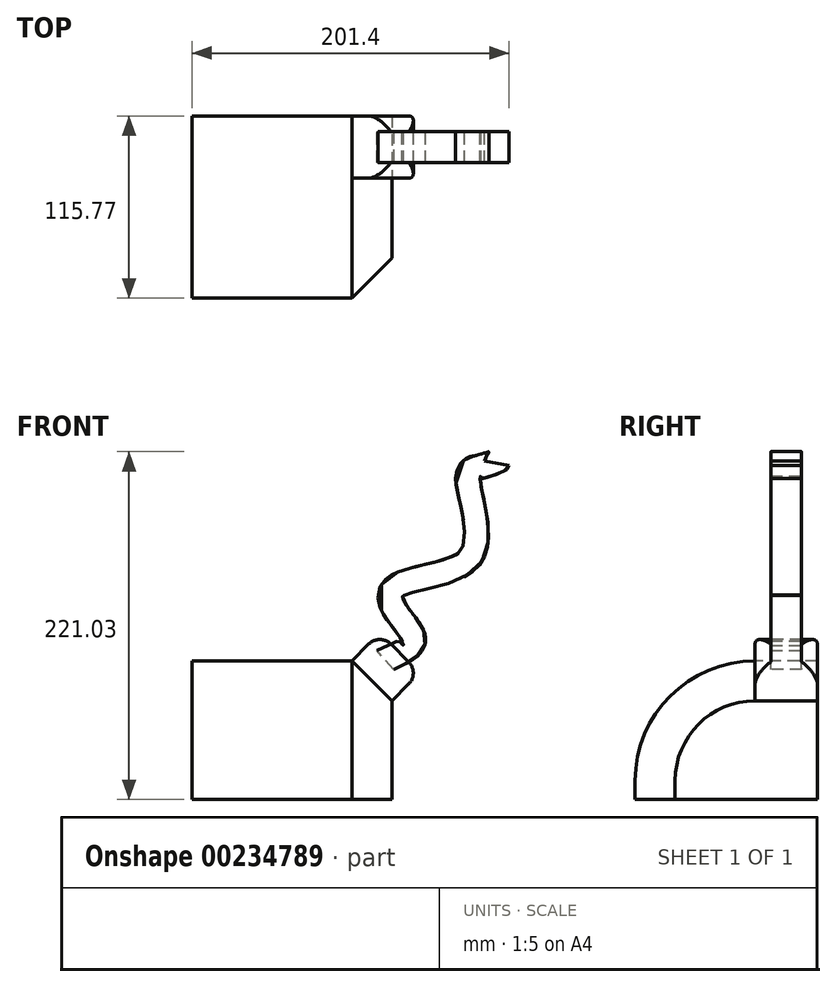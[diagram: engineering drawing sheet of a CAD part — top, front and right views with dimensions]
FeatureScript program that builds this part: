
annotation { "Feature Type Name" : "Feature", "Feature Type Description" : "" }
export const myFeature = defineFeature(function(context is Context, id is Id, definition is map)
    precondition{}
    {
        {
            var Q0;
            Q0=qCreatedBy(makeId("Top.planeOp"),FACE);
            var sketch = newSketch(context, id + "F0", { "sketchPlane" : qUnion([Q0])});
            skLineSegment(sketch, "E0.bottom", {"start": v(-62.89, 58.9) * mm, "end": v(64.11, 58.9) * mm});
            skLineSegment(sketch, "E0.top", {"start": v(-62.89, -56.86) * mm, "end": v(64.11, -56.86) * mm});
            skLineSegment(sketch, "E0.left", {"start": v(-62.89, 58.9) * mm, "end": v(-62.89, -56.86) * mm});
            skLineSegment(sketch, "E0.right", {"start": v(64.11, 58.9) * mm, "end": v(64.11, -56.86) * mm});
            skSolve(sketch);
        }
        {
            var Q0;
            Q0 = qSketchRegion(id + "F0", true);
            extrude(context, id + "F1", {"entities" : qUnion([Q0]), "depth" : 88.14 * mm});
        }
        {
            var Q0;
            Q0=makeQuery(id+"F1.opExtrude","CAP_EDGE",EDGE,{"disambiguationData":[OSD([sQuery(id+"F0.wireOp",EDGE,"E0.top")])],"isStart":false});
            fillet(context, id + "F2", {"entities" : qUnion([Q0]), "radius" : 76.2 * mm, "tangentPropagation" : true, "allowEdgeOverflow" : false});
        }
        {
            var Q0;
            Q0=makeQuery(id+"F1.opExtrude","CAP_EDGE",EDGE,{"disambiguationData":[OSD([sQuery(id+"F0.wireOp",EDGE,"E0.right")])],"isStart":false});
            chamfer(context, id + "F3", {"entities" : qUnion([Q0]), "width" : 25.4 * mm, "tangentPropagation" : true});
        }
        {
            var Q0;
            Q0=makeQuery(id+"F3.opChamfer","BLEND_FACE",FACE,{"disambiguationData":[OSD([sQuery(id+"F0.wireOp",EDGE,"E0.right")])]});
            extrude(context, id + "F4", {"entities" : qUnion([Q0]), "operationType" : NewBodyOperationType.ADD, "depth" : 25 * mm, "hasDraft" : true, "draftAngle" : 0 * degree});
        }
        {
            var Q0;
            Q0=makeQuery(id+"F4.opExtrude","CAP_EDGE",EDGE,{"disambiguationData":[OSD([sQuery(id+"F0.wireOp",EDGE,"E0.top"),sQuery(id+"F0.wireOp",EDGE,"E0.right")])],"isStart":false});
            var Q1;
            Q1=makeQuery(id+"F4.opExtrude","CAP_EDGE",EDGE,{"disambiguationData":[OSD([sQuery(id+"F0.wireOp",EDGE,"E0.right")])],"isStart":false});
            var Q2;
            Q2=makeQuery(id+"F4.opExtrude","CAP_EDGE",EDGE,{"disambiguationData":[OSD([sQuery(id+"F0.wireOp",EDGE,"E0.bottom"),sQuery(id+"F0.wireOp",EDGE,"E0.right")])],"isStart":false});
            var Q3;
            Q3=makeQuery(id+"F4.opExtrude","CAP_EDGE",EDGE,{"disambiguationData":[OSD([sQuery(id+"F0.wireOp",EDGE,"E0.bottom"),sQuery(id+"F0.wireOp",EDGE,"E0.top"),sQuery(id+"F0.wireOp",EDGE,"E0.left"),sQuery(id+"F0.wireOp",EDGE,"E0.right")])],"isStart":false});
            fillet(context, id + "F5", {"entities" : qUnion([Q0, Q1, Q2, Q3]), "radius" : 10 * mm, "tangentPropagation" : true, "allowEdgeOverflow" : false});
        }
        {
            var Q0;
            {var subQ0=sQuery(id+"F0.wireOp",EDGE,"E0.bottom");Q0=makeQuery(id+"F4.boolean.opBoolean","MERGE",FACE,{"derivedFrom":[makeQuery(id+"F1.opExtrude","SWEPT_FACE",FACE,{"disambiguationData":[OSD([subQ0])]}),makeQuery(id+"F4.opExtrude","SWEPT_FACE",FACE,{"disambiguationData":[OSD([subQ0,sQuery(id+"F0.wireOp",EDGE,"E0.right")])]})]});}
            var sketch = newSketch(context, id + "F6", { "sketchPlane" : qUnion([Q0])});
            skFitSpline(sketch, "E1", {"points": [v(-62.02, 86.04) * mm, v(-81.06, 102.94) * mm, v(-66.85, 130.18) * mm, v(-116.6, 152.22) * mm, v(-115.89, 204.81) * mm, v(-121.57, 208.37) * mm, v(-133.9, 212.87) * mm, v(-134.13, 213.1) * mm], "startDerivative": vector(-193.83, 87.36) * mm, "endDerivative": vector(-5.16, 10.28) * mm});
            skSolve(sketch);
        }
        {
            var Q0;
            Q0=makeQuery(id+"F4.opExtrude","CAP_FACE",FACE,{"disambiguationData":[OSD([sQuery(id+"F0.wireOp",EDGE,"E0.right")])],"isStart":false});
            var Q1;
            Q1=sQuery(id+"F6.wireOp",EDGE,"E1");
            sweep(context, id + "F7", {"profiles" : qUnion([Q0]), "path" : qUnion([Q1])});
        }
    });
